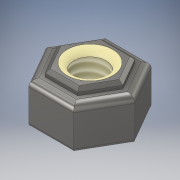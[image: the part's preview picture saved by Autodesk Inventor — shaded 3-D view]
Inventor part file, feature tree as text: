
AUTODESK INVENTOR PART (.ipt)
format: ipt  version: 2019 (Build 230136000, 136)  size: 181,248 bytes
history: native  units: in
note: dims shown in document units (in); Inventor stores cm internally (conversion verified against a paired STEP export)
features: fillet x3, sketch x3, extrude x2, chamfer x2, hole x1, thread x1, projected_geometry x1
ambient origin geometry x8: Origin, YZ Plane, XZ Plane, XY Plane, X Axis, Y Axis, Z Axis, Center Point
bodies: Solid1 (feature_tree)
feature tree (13):
  extrude  "Extrusion1"  Depth=0.23in TaperAngle=0.0deg
  extrude  "Extrusion2"  Depth=0.0312in TaperAngle=0.0deg
  fillet  "Fillet1"  Radius=0.0312in
  chamfer  "Chamfer1"  Distance=0.0156in Angle=45.0deg
  hole  "Hole1"  [1 undecoded]
  fillet  "Fillet2"  Radius=0.0312in
  thread  "Thread1"  [1 undecoded]
  chamfer  "Chamfer2"  Distance=0.0156in
  fillet  "Fillet3"  [1 undecoded]
  sketch  "Sketch1"  dims[d0=0.375in d1=0.23in d2=0.0in]
  sketch  "Sketch2"  dims[d3=0.05in d4=0.0312in d5=0.0in d6=0.0312in d7=0.0156in d8=0.125in d9=45.0deg]
  projected_geometry  "Projected Loop1"
  sketch  "Sketch3"  dims[d10=0.1562in d11=0.75in d12=0.375in d13=0.25in d14=0.5635in d15=1.0in d16=0.8108in d17=1.0in d18=0.0in d19=0.0312in d20=0.0156in d21=0.125in d22=45.0deg d23=0.0156in]
note: 3 required parameter values undecoded (feature->parameter linkage not recoverable at this tier; creation-order binding heuristic only, values carry confidence <= 0.55)
